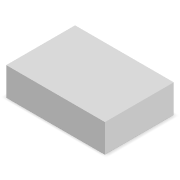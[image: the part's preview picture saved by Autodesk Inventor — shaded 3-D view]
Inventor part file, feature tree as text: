
AUTODESK INVENTOR PART (.ipt)
format: ipt  version: 2022 (Build 260153000, 153)  size: 73,728 bytes
history: native  units: mm
features: extrude x1, sketch x1
ambient origin geometry x8: Origin, YZ Plane, XZ Plane, XY Plane, X Axis, Y Axis, Z Axis, Center Point
bodies: Volumenkörper1 (feature_tree)
feature tree (2):
  extrude  "Extrusion1"  [1 undecoded]
  sketch  "Skizze1"  dims[d0=10.0mm d1=0.0mm]
note: 1 required parameter value undecoded (feature->parameter linkage not recoverable at this tier; creation-order binding heuristic only, values carry confidence <= 0.55)
